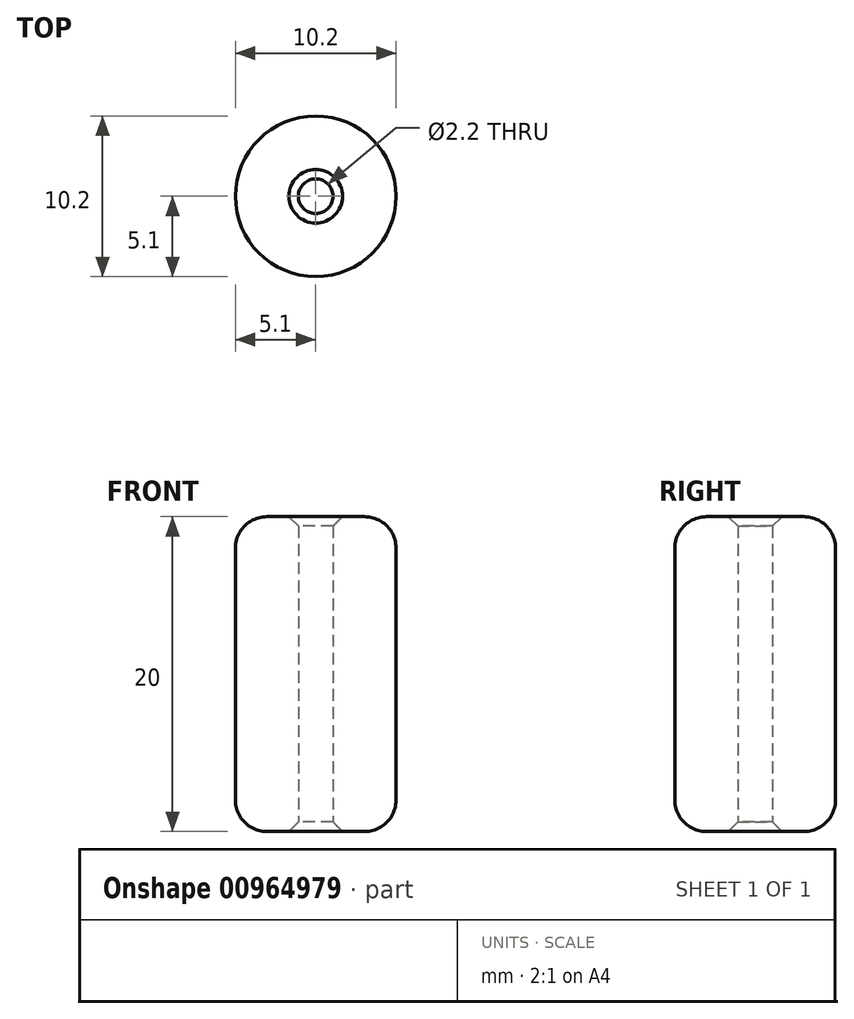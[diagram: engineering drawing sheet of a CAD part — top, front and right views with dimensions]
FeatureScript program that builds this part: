
annotation { "Feature Type Name" : "Feature", "Feature Type Description" : "" }
export const myFeature = defineFeature(function(context is Context, id is Id, definition is map)
    precondition{}
    {
        {
            var Q0;
            Q0=qCreatedBy(makeId("Top.planeOp"),FACE);
            var sketch = newSketch(context, id + "F0", { "sketchPlane" : qUnion([Q0])});
            skCircle(sketch, "E0", {"center": v(0, 0) * mm, "radius": 1.1 * mm});
            skCircle(sketch, "E1", {"center": v(0, 0) * mm, "radius": 5.1 * mm});
            skSolve(sketch);
        }
        {
            var Q0;
            Q0 = qSketchRegion(id + "F0", true);
            extrude(context, id + "F1", {"entities" : qUnion([Q0]), "depth" : 20 * mm, "offsetDistance" : 25.4 * mm});
        }
        {
            var Q0;
            Q0=makeQuery(id+"F1.opExtrude","CAP_EDGE",EDGE,{"disambiguationData":[OSD([sQuery(id+"F0.wireOp",EDGE,"E1")])],"isStart":false});
            var Q1;
            Q1=makeQuery(id+"F1.opExtrude","CAP_EDGE",EDGE,{"disambiguationData":[OSD([sQuery(id+"F0.wireOp",EDGE,"E1")])],"isStart":true});
            fillet(context, id + "F2", {"entities" : qUnion([Q0, Q1]), "radius" : 2 * mm, "tangentPropagation" : true, "allowEdgeOverflow" : false});
        }
        {
            var Q0;
            Q0=makeQuery(id+"F1.opExtrude","CAP_EDGE",EDGE,{"disambiguationData":[OSD([sQuery(id+"F0.wireOp",EDGE,"E0")])],"isStart":false});
            var Q1;
            Q1=makeQuery(id+"F1.opExtrude","CAP_EDGE",EDGE,{"disambiguationData":[OSD([sQuery(id+"F0.wireOp",EDGE,"E0")])],"isStart":true});
            chamfer(context, id + "F3", {"entities" : qUnion([Q0, Q1]), "width" : 0.6 * mm, "tangentPropagation" : true});
        }
    });
